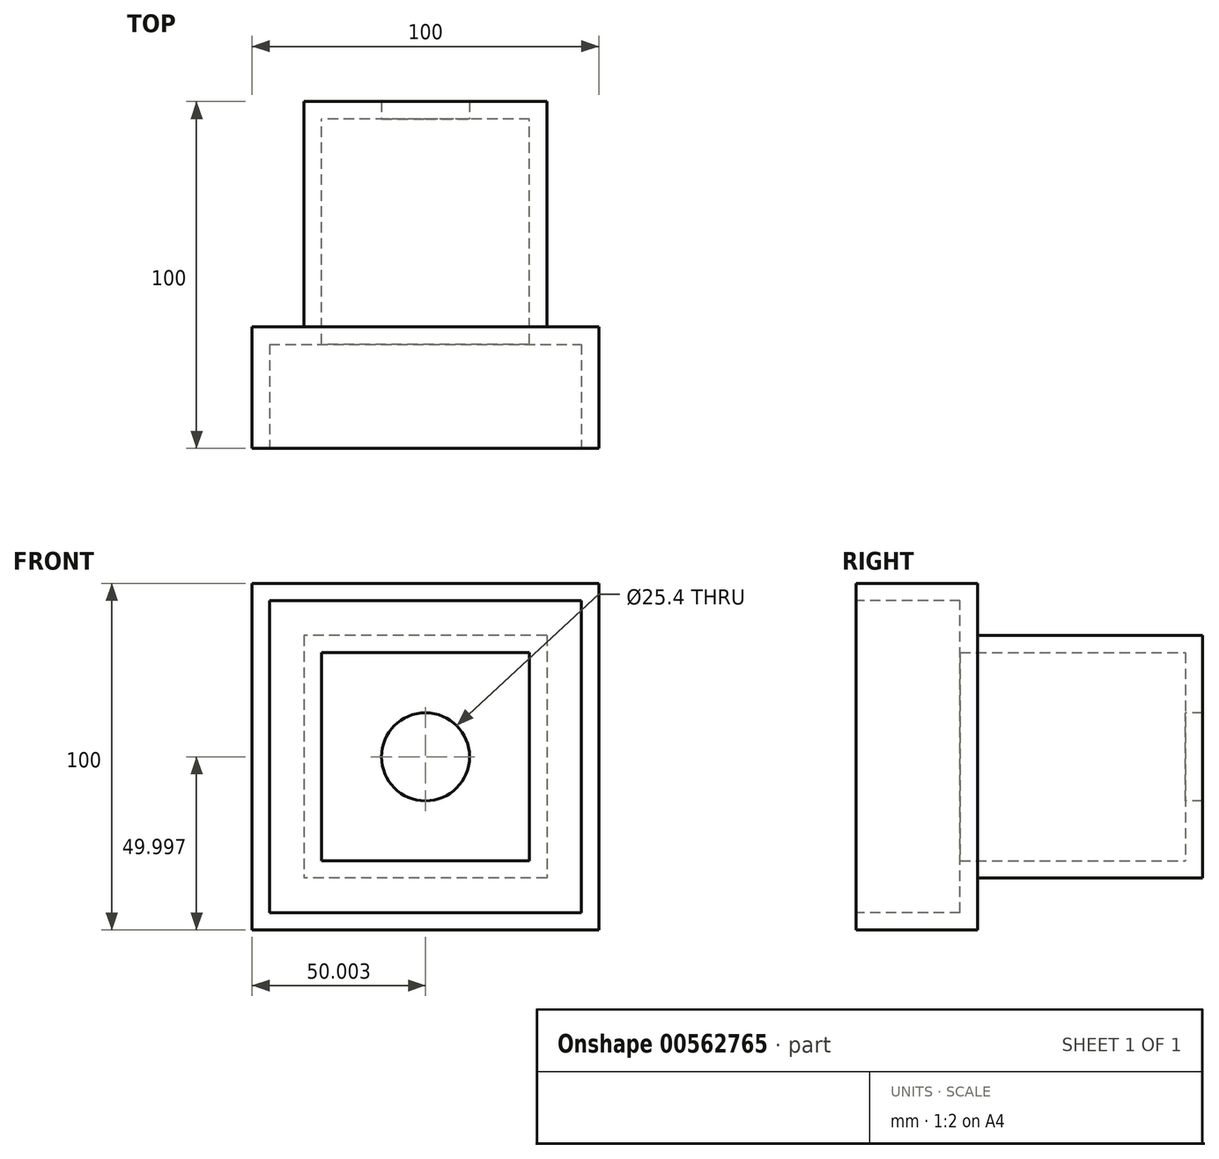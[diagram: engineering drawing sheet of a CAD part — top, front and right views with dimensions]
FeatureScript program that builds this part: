
annotation { "Feature Type Name" : "Feature", "Feature Type Description" : "" }
export const myFeature = defineFeature(function(context is Context, id is Id, definition is map)
    precondition{}
    {
        {
            var Q0;
            Q0=qCreatedBy(makeId("Right.planeOp"),FACE);
            cPlane(context, id + "F0", {"entities" : qUnion([Q0]), "cplaneType" : CPlaneType.OFFSET, "offset" : 76.48 * mm, "width" : 150 * mm, "height" : 150 * mm});
        }
        {
            var Q0;
            Q0=qCreatedBy(makeId("Top.planeOp"),FACE);
            var sketch = newSketch(context, id + "F1", { "sketchPlane" : qUnion([Q0])});
            skLineSegment(sketch, "E0", {"start": v(76.48, 640.4) * mm, "end": v(76.48, 514.42) * mm});
            skLineSegment(sketch, "E1", {"start": v(0, 638.15) * mm, "end": v(0, 512.18) * mm});
            skArc(sketch, "E2", {"start": v(0, 512.18) * mm, "mid": v(39.33, 476.17) * mm, "end": v(76.48, 514.42) * mm});
            skCircle(sketch, "E3", {"center": v(0, 638.15) * mm, "radius": 4.76 * mm});
            skCircle(sketch, "E4", {"center": v(76.48, 640.4) * mm, "radius": 4.76 * mm});
            skSolve(sketch);
        }
        {
            var Q0;
            Q0=qCreatedBy(makeId("Front.planeOp"),FACE);
            var sketch = newSketch(context, id + "F2", { "sketchPlane" : qUnion([Q0])});
            skCircle(sketch, "E5", {"center": v(0, 0) * mm, "radius": 4.76 * mm});
            skCircle(sketch, "E6", {"center": v(76.37, 0) * mm, "radius": 4.76 * mm});
            skSolve(sketch);
        }
        {
            var Q0;
            Q0=sQuery(id+"F2.wireOp",EDGE,"E6");
            var Q1;
            Q1=sQuery(id+"F1.wireOp",VERTEX,"E0.start");
            var Q2;
            Q2=sQuery(id+"F1.wireOp",VERTEX,"E2.end");
            extrude(context, id + "F3", {"bodyType" : ToolBodyType.SURFACE, "surfaceEntities" : qUnion([Q0]), "endBound" : BoundingType.UP_TO_VERTEX, "oppositeDirection" : true, "depth" : 25.4 * mm, "endBoundEntityVertex" : qUnion([Q1]), "offsetDistance" : 25.4 * mm, "hasSecondDirection" : true, "secondDirectionBound" : SecondDirectionBoundingType.UP_TO_VERTEX, "secondDirectionOppositeDirection" : true, "secondDirectionDepth" : 25.4 * mm, "secondDirectionBoundEntityVertex" : qUnion([Q2])});
        }
        {
            var Q0;
            Q0=qCreatedBy(id+"F0.planeOp",FACE);
            var sketch = newSketch(context, id + "F4", { "sketchPlane" : qUnion([Q0])});
            skFitSpline(sketch, "E7", {"points": [v(639.4, 0) * mm, v(649.2, 3.53) * mm, v(449.38, 405) * mm], "startDerivative": vector(94.17, -2.14) * mm, "endDerivative": vector(-362.28, 651.79) * mm});
            skSolve(sketch);
        }
        {
            var Q0;
            Q0=qCreatedBy(makeId("Right.planeOp"),FACE);
            var sketch = newSketch(context, id + "F5", { "sketchPlane" : qUnion([Q0])});
            skFitSpline(sketch, "E8", {"points": [v(638.15, 0) * mm, v(649, 3.53) * mm, v(449.19, 405) * mm], "startDerivative": vector(94.17, -2.14) * mm, "endDerivative": vector(-362.28, 651.79) * mm});
            skSolve(sketch);
        }
        {
            var Q0;
            Q0=sQuery(id+"F2.wireOp",EDGE,"E5");
            var Q1;
            Q1=sQuery(id+"F5.wireOp",VERTEX,"E8.start");
            var Q2;
            Q2=sQuery(id+"F1.wireOp",VERTEX,"E2.start");
            extrude(context, id + "F6", {"bodyType" : ToolBodyType.SURFACE, "surfaceEntities" : qUnion([Q0]), "endBound" : BoundingType.UP_TO_VERTEX, "oppositeDirection" : true, "depth" : 25.4 * mm, "endBoundEntityVertex" : qUnion([Q1]), "offsetDistance" : 25.4 * mm, "hasSecondDirection" : true, "secondDirectionBound" : SecondDirectionBoundingType.UP_TO_VERTEX, "secondDirectionOppositeDirection" : true, "secondDirectionDepth" : 25.4 * mm, "secondDirectionBoundEntityVertex" : qUnion([Q2])});
        }
        {
            var Q0;
            Q0=qCreatedBy(makeId("Front.planeOp"),FACE);
            cPlane(context, id + "F7", {"entities" : qUnion([Q0]), "cplaneType" : CPlaneType.OFFSET, "offset" : 290.14 * mm, "oppositeDirection" : true, "width" : 152.4 * mm, "height" : 152.4 * mm});
        }
        {
            var Q0;
            Q0=qCreatedBy(id+"F7.planeOp",FACE);
            cPlane(context, id + "F8", {"entities" : qUnion([Q0]), "cplaneType" : CPlaneType.OFFSET, "offset" : 116.54 * mm, "oppositeDirection" : true, "width" : 152.4 * mm, "height" : 152.4 * mm});
        }
        {
            var Q0;
            Q0=qCreatedBy(id+"F8.planeOp",FACE);
            cPlane(context, id + "F9", {"entities" : qUnion([Q0]), "cplaneType" : CPlaneType.OFFSET, "offset" : 100 * mm, "oppositeDirection" : true, "width" : 152.4 * mm, "height" : 152.4 * mm});
        }
        {
            var Q0;
            Q0=qCreatedBy(id+"F8.planeOp",FACE);
            var sketch = newSketch(context, id + "F10", { "sketchPlane" : qUnion([Q0])});
            skLineSegment(sketch, "E9.bottom", {"start": v(-12.45, 367.72) * mm, "end": v(87.55, 367.72) * mm});
            skLineSegment(sketch, "E9.top", {"start": v(-12.45, 467.72) * mm, "end": v(87.55, 467.72) * mm});
            skLineSegment(sketch, "E9.left", {"start": v(-12.45, 367.72) * mm, "end": v(-12.45, 467.72) * mm});
            skLineSegment(sketch, "E9.right", {"start": v(87.55, 367.72) * mm, "end": v(87.55, 467.72) * mm});
            skPoint(sketch, "E9.middle", {"position": v(37.55, 417.72) * mm});
            skSolve(sketch);
        }
        {
            var Q0;
            Q0=qCreatedBy(id+"F8.planeOp",FACE);
            cPlane(context, id + "F11", {"entities" : qUnion([Q0]), "cplaneType" : CPlaneType.OFFSET, "offset" : 35 * mm, "oppositeDirection" : true, "width" : 152.4 * mm, "height" : 152.4 * mm});
        }
        {
            var Q0;
            Q0=qCreatedBy(id+"F11.planeOp",FACE);
            var sketch = newSketch(context, id + "F12", { "sketchPlane" : qUnion([Q0])});
            skLineSegment(sketch, "E10.bottom", {"start": v(87.55, 367.72) * mm, "end": v(-12.45, 367.72) * mm});
            skLineSegment(sketch, "E10.top", {"start": v(87.55, 467.72) * mm, "end": v(-12.45, 467.72) * mm});
            skLineSegment(sketch, "E10.left", {"start": v(87.55, 367.72) * mm, "end": v(87.55, 467.72) * mm});
            skLineSegment(sketch, "E10.right", {"start": v(-12.45, 367.72) * mm, "end": v(-12.45, 467.72) * mm});
            skPoint(sketch, "E10.middle", {"position": v(37.55, 417.72) * mm});
            skLineSegment(sketch, "E11.bottom", {"start": v(72.55, 382.72) * mm, "end": v(2.55, 382.72) * mm});
            skLineSegment(sketch, "E11.top", {"start": v(72.55, 452.72) * mm, "end": v(2.55, 452.72) * mm});
            skLineSegment(sketch, "E11.left", {"start": v(72.55, 382.72) * mm, "end": v(72.55, 452.72) * mm});
            skLineSegment(sketch, "E11.right", {"start": v(2.55, 382.72) * mm, "end": v(2.55, 452.72) * mm});
            skSolve(sketch);
        }
        {
            var Q0;
            Q0=qCreatedBy(id+"F9.planeOp",FACE);
            var sketch = newSketch(context, id + "F13", { "sketchPlane" : qUnion([Q0])});
            skLineSegment(sketch, "E12.bottom", {"start": v(72.55, 452.72) * mm, "end": v(2.55, 452.72) * mm});
            skLineSegment(sketch, "E12.top", {"start": v(72.55, 382.72) * mm, "end": v(2.55, 382.72) * mm});
            skLineSegment(sketch, "E12.left", {"start": v(72.55, 452.72) * mm, "end": v(72.55, 382.72) * mm});
            skLineSegment(sketch, "E12.right", {"start": v(2.55, 452.72) * mm, "end": v(2.55, 382.72) * mm});
            skPoint(sketch, "E12.middle", {"position": v(37.55, 417.72) * mm});
            skSolve(sketch);
        }
        {
            var Q0;
            Q0=makeQuery(id+"F10.imprint","IMPRINT",FACE,{"disambiguationData":[TD([[makeQuery(id+"F10.imprint","IMPRINT",EDGE,{"derivedFrom":sQuery(id+"F10.wireOp",EDGE,"E9.bottom")}),1.0]])]});
            var Q1;
            Q1=sQuery(id+"F12.wireOp",VERTEX,"E10.middle");
            extrude(context, id + "F14", {"entities" : qUnion([Q0]), "endBound" : BoundingType.UP_TO_VERTEX, "oppositeDirection" : true, "depth" : 25.4 * mm, "endBoundEntityVertex" : qUnion([Q1]), "offsetDistance" : 25.4 * mm});
        }
        {
            var Q0;
            Q0=makeQuery(id+"F13.imprint","IMPRINT",FACE,{"disambiguationData":[TD([[makeQuery(id+"F13.imprint","IMPRINT",EDGE,{"derivedFrom":sQuery(id+"F13.wireOp",EDGE,"E12.bottom")}),1.0]])]});
            var Q1;
            Q1=sQuery(id+"F12.wireOp",VERTEX,"E10.middle");
            extrude(context, id + "F15", {"entities" : qUnion([Q0]), "operationType" : NewBodyOperationType.ADD, "endBound" : BoundingType.UP_TO_VERTEX, "depth" : 25.4 * mm, "endBoundEntityVertex" : qUnion([Q1]), "offsetDistance" : 25.4 * mm});
        }
        {
            var Q0;
            Q0=makeQuery(id+"F14.opExtrude","CAP_FACE",FACE,{"disambiguationData":[OSD([sQuery(id+"F10.wireOp",EDGE,"E9.bottom"),sQuery(id+"F10.wireOp",EDGE,"E9.top"),sQuery(id+"F10.wireOp",EDGE,"E9.left"),sQuery(id+"F10.wireOp",EDGE,"E9.right")])],"isStart":true});
            shell(context, id + "F16", {"entities" : qUnion([Q0]), "thickness" : 5 * mm});
        }
        {
            var Q0;
            Q0=qCreatedBy(id+"F0.planeOp",FACE);
            var sketch = newSketch(context, id + "F17", { "sketchPlane" : qUnion([Q0])});
            skCircle(sketch, "E13", {"center": v(449.24, 404.98) * mm, "radius": 4.96 * mm});
            skSolve(sketch);
        }
        {
            var Q0;
            Q0=sQuery(id+"F17.wireOp",EDGE,"E13");
            extrude(context, id + "F18", {"bodyType" : ToolBodyType.SURFACE, "surfaceEntities" : qUnion([Q0]), "endBound" : BoundingType.SYMMETRIC, "depth" : 33.02 * mm, "offsetDistance" : 25.4 * mm});
        }
        {
            var Q0;
            Q0=qCreatedBy(makeId("Right.planeOp"),FACE);
            var sketch = newSketch(context, id + "F19", { "sketchPlane" : qUnion([Q0])});
            skCircle(sketch, "E14", {"center": v(449.15, 405.06) * mm, "radius": 4.98 * mm});
            skSolve(sketch);
        }
        {
            var Q0;
            Q0=sQuery(id+"F19.wireOp",EDGE,"E14");
            extrude(context, id + "F20", {"bodyType" : ToolBodyType.SURFACE, "surfaceEntities" : qUnion([Q0]), "endBound" : BoundingType.SYMMETRIC, "depth" : 33.02 * mm, "offsetDistance" : 25.4 * mm});
        }
        {
            var Q0;
            Q0=sQuery(id+"F12.wireOp",VERTEX,"E10.middle");
            var Q1;
            Q1=makeQuery(id+"F14.opExtrude","SWEPT_BODY",BODY,{"disambiguationData":[OSD([sQuery(id+"F10.wireOp",EDGE,"E9.bottom"),sQuery(id+"F10.wireOp",EDGE,"E9.top"),sQuery(id+"F10.wireOp",EDGE,"E9.left"),sQuery(id+"F10.wireOp",EDGE,"E9.right")])]});
            hole(context, id + "F21", {"style" : HoleStyle.SIMPLE, "endStyle" : HoleEndStyle.THROUGH, "holeDiameter" : 25.4 * mm, "isTappedThrough" : true, "tappedDepth" : 12.7 * mm, "tapClearance" : 3, "locations" : qUnion([Q0]), "scope" : qUnion([Q1])});
        }
    });
